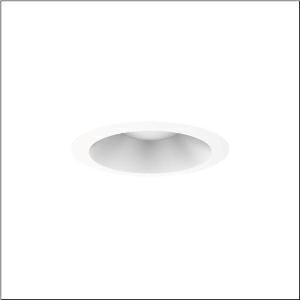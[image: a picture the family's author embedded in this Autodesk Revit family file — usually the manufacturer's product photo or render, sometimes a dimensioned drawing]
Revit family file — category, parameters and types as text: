
# Revit family: lunis_31_midi_51dn15dg42
name_source: partatom
category: Lighting Fixtures
units: mm (PartAtom-declared; Revit-internal decimal feet)

## family parameters
Cut with Voids When Loaded = No
Host = Face
Light Source = No
Part Type = Normal
Room Calculation Point = No
Round Connector Dimension = Use Diameter
Shared = No

## types (1)
- Lunis 31 midi (1 x LED, 2150 lm, 17 W, 4000K)
    Apparent Load = 17 VA
    CIE Flux Codes = 89 99 100 100 100
    Color Rendering = 80
    Color Temperature = 4000K
    Default Elevation = 1800 mm
    Description = Lunis 31,  midi, downlight, light control with lens, light emission: direct distribution, LED rated luminous flux: 2.150lm, light colour: 840, mains connection: 220..240V, AC, 50/60Hz, housing, white, protection rating (complete): IP20, protection rating (on room side): IP54, insulation class (complete): insulation class II (safety insulation), certification: CE, packaging unit: 1 piece
    Height = 0 mm  [stored 0 ft]
    Lamp = 1 x LED
    Lamp Light Flux = 2150 lm
    Lamp Power = 17 W
    Lamp count = 1
    Length = 259 mm
    Luminous efficacy = 126 lm/W
    Manufacturer = Siteco
    ModVariant = No
    Model = 51DN15DG42
    Mounting Place = Ceiling
    Mounting Type = Recessed
    Number of Poles = 1
    OnlyDefault = Yes
    Power Factor = 1
    Product Name = Lunis 31 midi
    Product group = downlight
    ProductGroupID = 400
    Protection Class = Protection class II
    Protection Degree = IP 20
    RLX_Detail_Level = 1
    RLX_Emergency_Light_Flux = 0 lm
    RLX_Emergency_Type = 0
    RLX_Emergency_Type_DB = No
    RlxData = <blob elided: 23645 chars, md5=5875d502>
    Socket = socket
    Standby Power = 0 W
    System Light Flux = 2150 lm
    System Power = 17 W
    Type Comments = Product without accessories
    Type Image = l_1006711.jpg
    URL = http://relux.com
    VarID = ---
    Voltage = 0 V
    Weight = 0.00 kg
    Width = 0 mm  [stored 0 ft]

note: [stored X ft] marks values corroborated as IEEE doubles in the binary element streams (Revit-internal decimal feet)

## geometry (parser evidence)
native form markers: Blend x4, Sweep x11
no freeform markers — native parametric forms only
